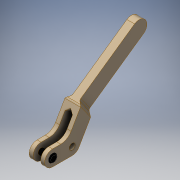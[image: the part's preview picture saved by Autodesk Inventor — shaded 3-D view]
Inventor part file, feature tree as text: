
AUTODESK INVENTOR PART (.ipt)
format: ipt  version: 2018.1 (Build 221151000, 151)  size: 250,880 bytes
history: native  units: in
note: dims shown in document units (in); Inventor stores cm internally (conversion verified against a paired STEP export)
features: sketch x4, extrude x4, fillet x2, plane x2, chamfer x1, hole x1, other x1, revolve x1
ambient origin geometry x8: Origin, YZ Plane, XZ Plane, XY Plane, X Axis, Y Axis, Z Axis, Center Point
bodies: Solid3 (feature_tree), Solid4 (feature_tree)
feature tree (16):
  sketch  "Sketch1"  dims[d0=0.25in d2=0.625in]
  extrude  "Extrusion2"  Depth=0.625in
  extrude  "Extrusion3"  Depth=2.88in
  extrude  "Extrusion7"  Depth=0.9963in
  chamfer  "Chamfer1"  Distance=0.244in
  fillet  "Fillet4"  Radius=0.494in
  plane  "Work Plane4"
  hole  "Hole1"  [1 undecoded]
  other  "Work Axis1"
  plane  "Work Plane1"
  revolve  "Revolution1"  Angle=45.0deg
  extrude  "Extrusion8"  Depth=0.125in
  fillet  "Fillet5"  Radius=0.189in
  sketch  "Sketch5"  dims[d3=2.06in d4=2.88in]
  sketch  "Sketch7"  dims[d6=0.1718in d7=0.9963in]
  sketch  "Sketch8"  dims[d8=0.4994in d15=0.244in d16=0.0in d17=0.494in d18=0.0in d43=0.494in d44=0.0in d45=0.125in d46=0.125in d47=45.0deg d48=0.1in d49=0.189in d51=0.25in d52=0.018in d53=0.625in d54=0.2677in d55=0.189in d56=0.75in d57=0.375in d58=0.25in d59=0.5635in d60=1.0in d61=0.8108in d62=0.0394in d64=0.0945in d65=0.5727in d66=0.2864in d68=0.0945in d69=0.0in d70=0.0394in d71=90.0deg d72=45.0deg d73=0.119in d75=0.238in d76=1.39in d80=0.366in d81=1.0in d82=0.0in d83=0.125in]
note: 1 required parameter value undecoded (feature->parameter linkage not recoverable at this tier; creation-order binding heuristic only, values carry confidence <= 0.55)
